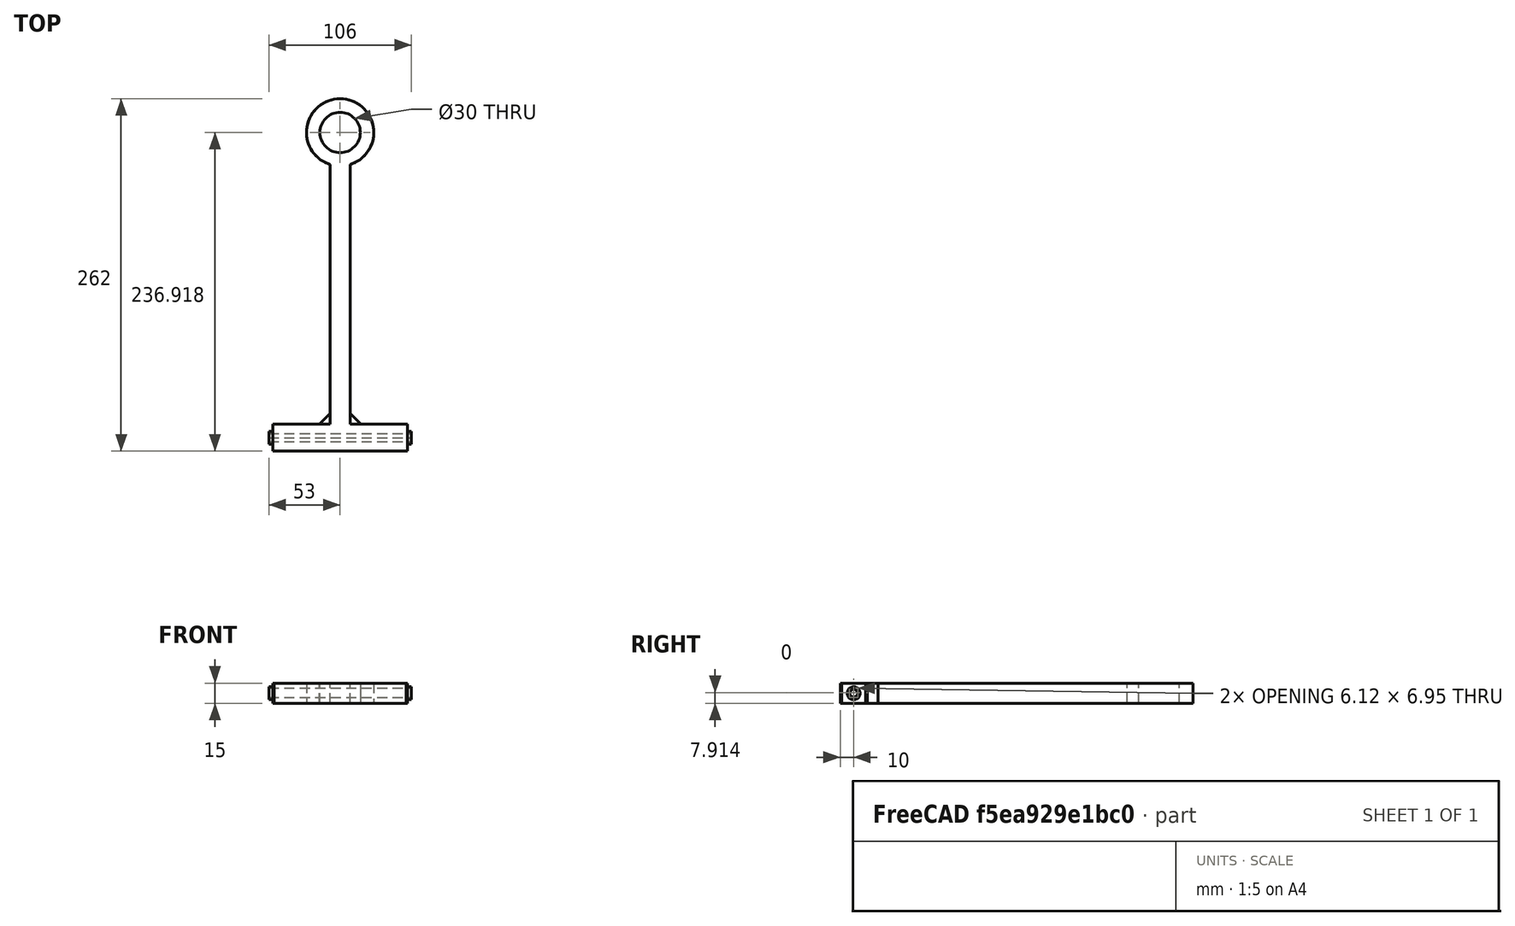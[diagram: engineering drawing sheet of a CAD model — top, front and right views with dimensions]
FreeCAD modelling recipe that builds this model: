
FCSTD DOCUMENT  (FreeCAD 0.16R)
Label: TireSpacer50mm-505
License: All rights reserved
LicenseURL: http://en.wikipedia.org/wiki/All_rights_reserved
objects: Sketcher::SketchObject×4, PartDesign::Pad×2, PartDesign::Pocket×2, PartDesign::Fillet×2, PartDesign::Chamfer×2, Mesh::Feature×1
note: 16 computed .brp shape members not serialized (recipe doc carries the construction recipe); baked Part::Feature solids carry a one-line shape summary decoded from their .brp

FEATURE [Sketcher::SketchObject] Sketch
  sketch-geometry (9):
    g0: ArcOfCircle CenterX=0 CenterY=227 CenterZ=0 NormalX=0 NormalY=0 NormalZ=1 Radius=25 StartAngle=5.01708 EndAngle=10.6909
    g1: LineSegment [constr] StartX=-40 StartY=252 StartZ=0 EndX=40 EndY=252 EndZ=0
    g2: LineSegment StartX=-7.5 StartY=203.152 StartZ=0 EndX=-7.5 EndY=10 EndZ=0
    g3: LineSegment StartX=7.5 StartY=203.152 StartZ=0 EndX=7.5 EndY=10 EndZ=0
    g4: LineSegment StartX=50 StartY=10 StartZ=0 EndX=50 EndY=-10 EndZ=0
    g5: LineSegment StartX=50 StartY=-10 StartZ=0 EndX=-50 EndY=-10 EndZ=0
    g6: LineSegment StartX=-50 StartY=-10 StartZ=0 EndX=-50 EndY=10 EndZ=0
    g7: LineSegment StartX=-50 StartY=10 StartZ=0 EndX=-7.5 EndY=10 EndZ=0
    g8: LineSegment StartX=7.5 StartY=10 StartZ=0 EndX=50 EndY=10 EndZ=0
  constraints (28):
    c: Radius(g0) = 25
    c: Tangent(g1,g0)
    c: Horizontal(g1)
    c: Symmetric(g1,g1,g-2)
    c: PointOnObject(g0,g-2)
    c: DistanceY(g1) = 252
    c: Vertical(g2)
    c: Vertical(g3)
    c: Coincident(g4,g5)
    c: Coincident(g5,g6)
    c: Horizontal(g5)
    c: Vertical(g4)
    c: Vertical(g6)
    c: Symmetric(g4,g6,g-2)
    c: Coincident(g7,g6)
    c: Coincident(g7,g2)
    c: Coincident(g8,g3)
    c: Coincident(g8,g4)
    c: Horizontal(g7)
    c: Horizontal(g8)
    c: Distance(g4,g6) = 100
    c: DistanceY(g4) = -10
    c: Coincident(g0,g3)
    c: Coincident(g0,g2)
    c: Symmetric(g0,g0,g-2)
    c: Distance(g0,g0) = 15
    c: DistanceY(g4) = 10
    c: Distance(g1) = 80
FEATURE [PartDesign::Pad] Pad
  Length = 15
  Length2 = 100
  Midplane = true
  Sketch = -> Sketch
  Type = 0
FEATURE [Sketcher::SketchObject] Sketch002
  Placement = pos=(-50,0,0) rot=(0.57735,-0.57735,-0.57735;2.0944rad)
  Support = -> Pad [Face5]
  sketch-geometry (1):
    g0: Circle CenterX=0 CenterY=0 CenterZ=0 NormalX=0 NormalY=0 NormalZ=1 Radius=4.8
  constraints (2):
    c: Radius(g0) = 4.8
    c: Coincident(g0,g-1)
FEATURE [PartDesign::Pad] Pad001
  Length = 3
  Length2 = 103
  Sketch = -> Sketch002
  Type = 4
FEATURE [Sketcher::SketchObject] Sketch001
  Placement = pos=(-53,0,0) rot=(0.57735,-0.57735,-0.57735;2.0944rad)
  Support = -> Pad001 [Face14]
  sketch-geometry (4):
    g0: LineSegment StartX=-3.88909 StartY=0 StartZ=0 EndX=0 EndY=3.88909 EndZ=0
    g1: LineSegment StartX=0 StartY=3.88909 StartZ=0 EndX=3.88909 EndY=0 EndZ=0
    g2: LineSegment StartX=3.88909 StartY=0 StartZ=0 EndX=0 EndY=-3.88909 EndZ=0
    g3: LineSegment StartX=0 StartY=-3.88909 StartZ=0 EndX=-3.88909 EndY=0 EndZ=0
  constraints (11):
    c: Coincident(g0,g1)
    c: Coincident(g1,g2)
    c: Coincident(g2,g3)
    c: Coincident(g3,g0)
    c: Equal(g3,g0)
    c: Equal(g0,g1)
    c: Equal(g1,g2)
    c: Perpendicular(g1,g2)
    c: Distance(g2) = 5.5
    c: Symmetric(g0,g1,g-1)
    c: Angle(g1) = -0.785398
FEATURE [PartDesign::Pocket] Pocket
  Length = 5
  Sketch = -> Sketch001
  Type = 1
FEATURE [PartDesign::Fillet] Fillet
  Base = -> Pocket [Edge41,Edge40,Edge42]
  Radius = 2
FEATURE [Sketcher::SketchObject] Sketch003
  Placement = pos=(0,0,7.5) rot=(0,0,1;0rad)
  Support = -> Fillet [Face15]
  sketch-geometry (1):
    g0: Circle CenterX=0 CenterY=226.918 CenterZ=0 NormalX=0 NormalY=0 NormalZ=1 Radius=15
  constraints (2):
    c: Radius(g0) = 15
    c: PointOnObject(g0,g-2)
FEATURE [PartDesign::Pocket] Pocket001
  Length = 5
  Sketch = -> Sketch003
  Type = 1
FEATURE [PartDesign::Chamfer] Chamfer
  Base = -> Pocket001 [Edge32,Edge53]
  Size = 8
FEATURE [PartDesign::Chamfer] Chamfer001
  Base = -> Chamfer [Edge3,Edge18,Edge33,Edge32]
  Size = 1
FEATURE [PartDesign::Fillet] Fillet001
  Base = -> Chamfer001 [Edge39,Edge37]
  Radius = 2
FEATURE [Mesh::Feature] Mesh  label="Fillet001 (Meshed)"
